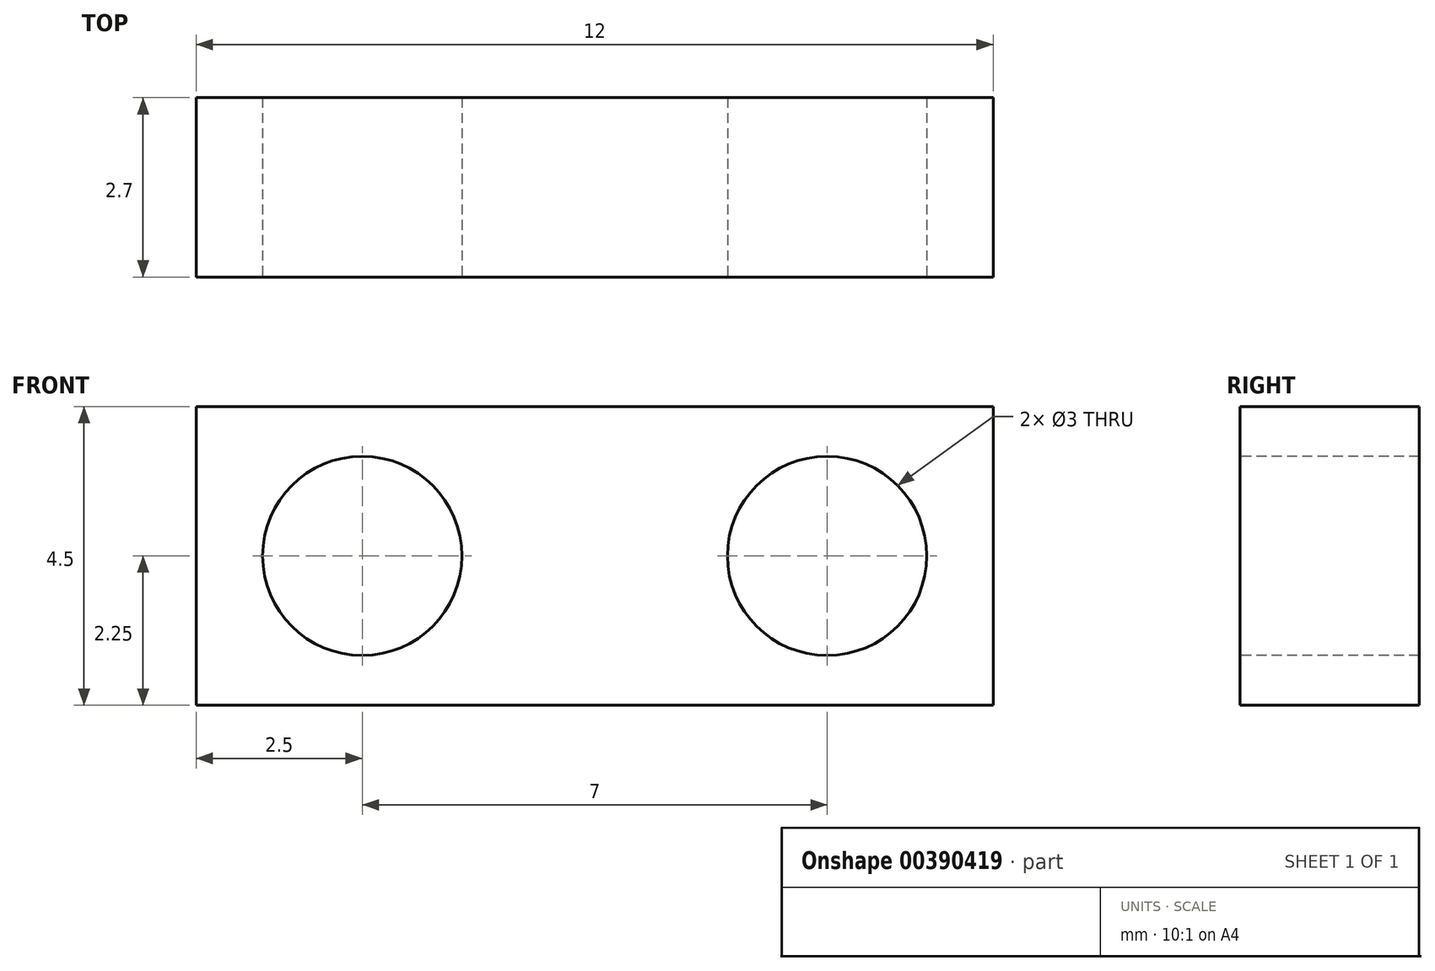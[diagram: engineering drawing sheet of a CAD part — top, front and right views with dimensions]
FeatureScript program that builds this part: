
annotation { "Feature Type Name" : "Feature", "Feature Type Description" : "" }
export const myFeature = defineFeature(function(context is Context, id is Id, definition is map)
    precondition{}
    {
        {
            var Q0;
            Q0=qCreatedBy(makeId("Front.planeOp"),FACE);
            var sketch = newSketch(context, id + "F0", { "sketchPlane" : qUnion([Q0])});
            skLineSegment(sketch, "E0.bottom", {"start": v(6, 2.25) * mm, "end": v(-6, 2.25) * mm});
            skLineSegment(sketch, "E0.top", {"start": v(6, -2.25) * mm, "end": v(-6, -2.25) * mm});
            skLineSegment(sketch, "E0.left", {"start": v(6, 2.25) * mm, "end": v(6, -2.25) * mm});
            skLineSegment(sketch, "E0.right", {"start": v(-6, 2.25) * mm, "end": v(-6, -2.25) * mm});
            skPoint(sketch, "E0.middle", {"position": v(0, 0) * mm});
            skSolve(sketch);
        }
        {
            var Q0;
            Q0=qSketchRegion(id+"F0",true);
            extrude(context, id + "F1", {"entities" : qUnion([Q0]), "depth" : (3 - .3) * mm});
        }
        {
            var Q0;
            Q0=makeQuery(id+"F1.opExtrude","CAP_FACE",FACE,{"disambiguationData":[OSD([sQuery(id+"F0.wireOp",EDGE,"E0.bottom"),sQuery(id+"F0.wireOp",EDGE,"E0.top"),sQuery(id+"F0.wireOp",EDGE,"E0.left"),sQuery(id+"F0.wireOp",EDGE,"E0.right")])],"isStart":false});
            var sketch = newSketch(context, id + "F2", { "sketchPlane" : qUnion([Q0])});
            skCircle(sketch, "E1", {"center": v(-3.5, 0) * mm, "radius": 1.5 * mm});
            skCircle(sketch, "E2", {"center": v(3.5, 0) * mm, "radius": 1.5 * mm});
            skLineSegment(sketch, "E3", {"start": v(-2, 0) * mm, "end": v(2, 0) * mm});
            skPoint(sketch, "E4", {"position": v(0, 0) * mm});
            skSolve(sketch);
        }
        {
            var Q0;
            Q0=makeQuery(id+"F2.imprint","IMPRINT",FACE,{"disambiguationData":[TD([[makeQuery(id+"F2.imprint","IMPRINT",EDGE,{"derivedFrom":sQuery(id+"F2.wireOp",EDGE,"E1")}),1.0]])]});
            var Q1;
            Q1=makeQuery(id+"F2.imprint","IMPRINT",FACE,{"disambiguationData":[TD([[makeQuery(id+"F2.imprint","IMPRINT",EDGE,{"derivedFrom":sQuery(id+"F2.wireOp",EDGE,"E2")}),1.0]])]});
            extrude(context, id + "F3", {"entities" : qUnion([Q0, Q1]), "operationType" : NewBodyOperationType.REMOVE, "oppositeDirection" : true, "depth" : 25 * mm});
        }
    });
